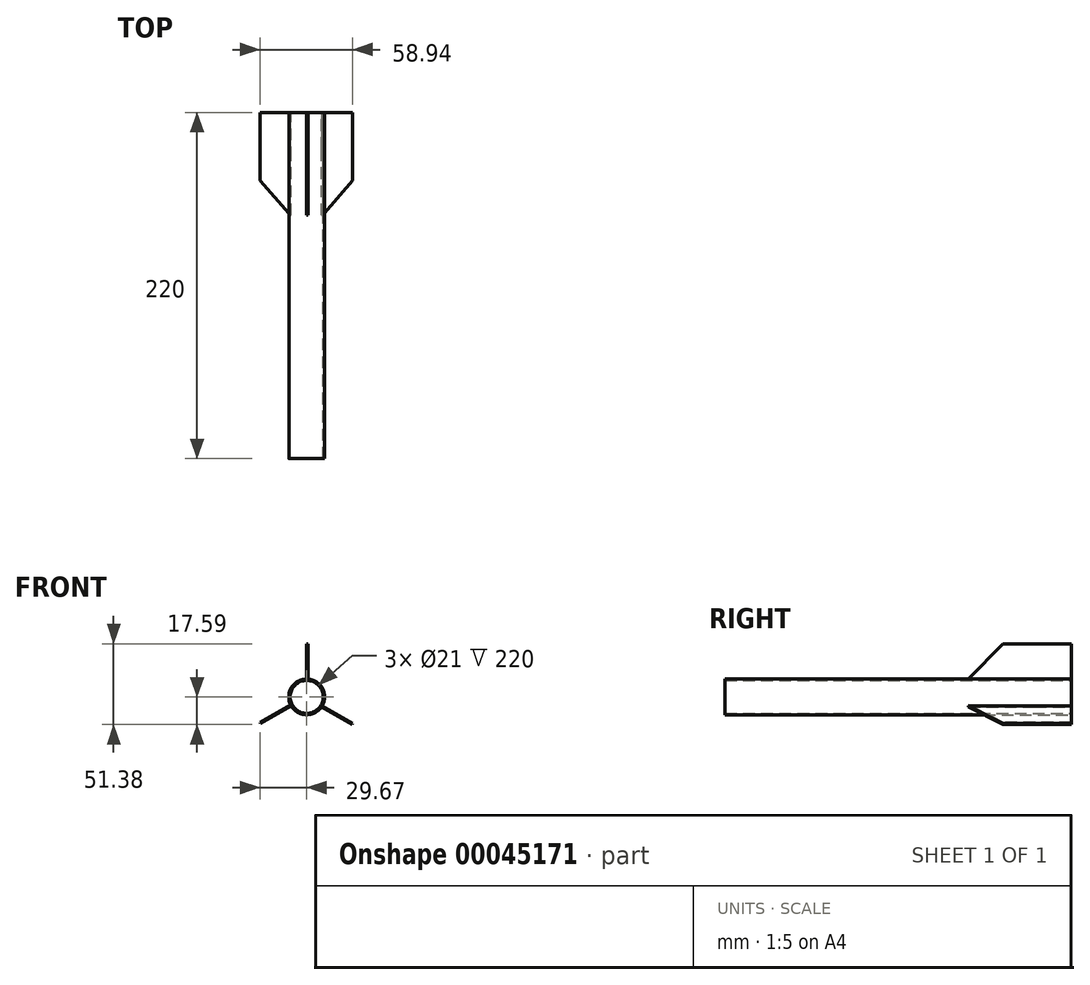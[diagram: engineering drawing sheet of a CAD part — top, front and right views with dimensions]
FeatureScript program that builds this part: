
annotation { "Feature Type Name" : "Feature", "Feature Type Description" : "" }
export const myFeature = defineFeature(function(context is Context, id is Id, definition is map)
    precondition{}
    {
        {
            var Q0;
            Q0=qCreatedBy(makeId("Front.planeOp"),FACE);
            var sketch = newSketch(context, id + "F0", { "sketchPlane" : qUnion([Q0])});
            skCircle(sketch, "E0", {"center": v(0, 0) * mm, "radius": 11.3 * mm});
            skCircle(sketch, "E1", {"center": v(0, 0) * mm, "radius": 10.5 * mm});
            skSolve(sketch);
        }
        {
            var Q0;
            Q0=makeQuery(id+"F0.imprint","IMPRINT",FACE,{"disambiguationData":[TD([[makeQuery(id+"F0.imprint","IMPRINT",EDGE,{"derivedFrom":sQuery(id+"F0.wireOp",EDGE,"E0")}),1.0]])]});
            extrude(context, id + "F1", {"entities" : qUnion([Q0]), "depth" : 220 * mm});
        }
        {
            var Q0;
            Q0=qCreatedBy(makeId("Right.planeOp"),FACE);
            var sketch = newSketch(context, id + "F2", { "sketchPlane" : qUnion([Q0])});
            skLineSegment(sketch, "E2", {"start": v(0, 11.16) * mm, "end": v(0, 33.8) * mm});
            skLineSegment(sketch, "E3", {"start": v(0, 33.8) * mm, "end": v(-43.36, 33.8) * mm});
            skLineSegment(sketch, "E4", {"start": v(-43.36, 33.8) * mm, "end": v(-65.37, 11.47) * mm});
            skLineSegment(sketch, "E5", {"start": v(-65.37, 11.47) * mm, "end": v(0, 11.16) * mm});
            skSolve(sketch);
        }
        {
            var Q0;
            Q0=makeQuery(id+"F2.imprint","IMPRINT",FACE,{"disambiguationData":[TD([[makeQuery(id+"F2.imprint","IMPRINT",EDGE,{"derivedFrom":sQuery(id+"F2.wireOp",EDGE,"E2")}),1.0]])]});
            extrude(context, id + "F3", {"entities" : qUnion([Q0]), "operationType" : NewBodyOperationType.ADD, "depth" : 0.8 * mm});
        }
        {
            var Q0;
            Q0=makeQuery(id+"F1.opExtrude","SWEPT_BODY",BODY,{"disambiguationData":[OSD([sQuery(id+"F0.wireOp",EDGE,"E0"),sQuery(id+"F0.wireOp",EDGE,"E1")])]});
            var Q1;
            Q1=makeQuery(id+"F1.opExtrude","SWEPT_FACE",FACE,{"disambiguationData":[OSD([sQuery(id+"F0.wireOp",EDGE,"E0")])]});
            circularPattern(context, id + "F4", {"entities" : qUnion([Q0]), "axis" : qUnion([Q1]), "angle" : 360 * degree, "instanceCount" : 3, "equalSpace" : true});
        }
    });
